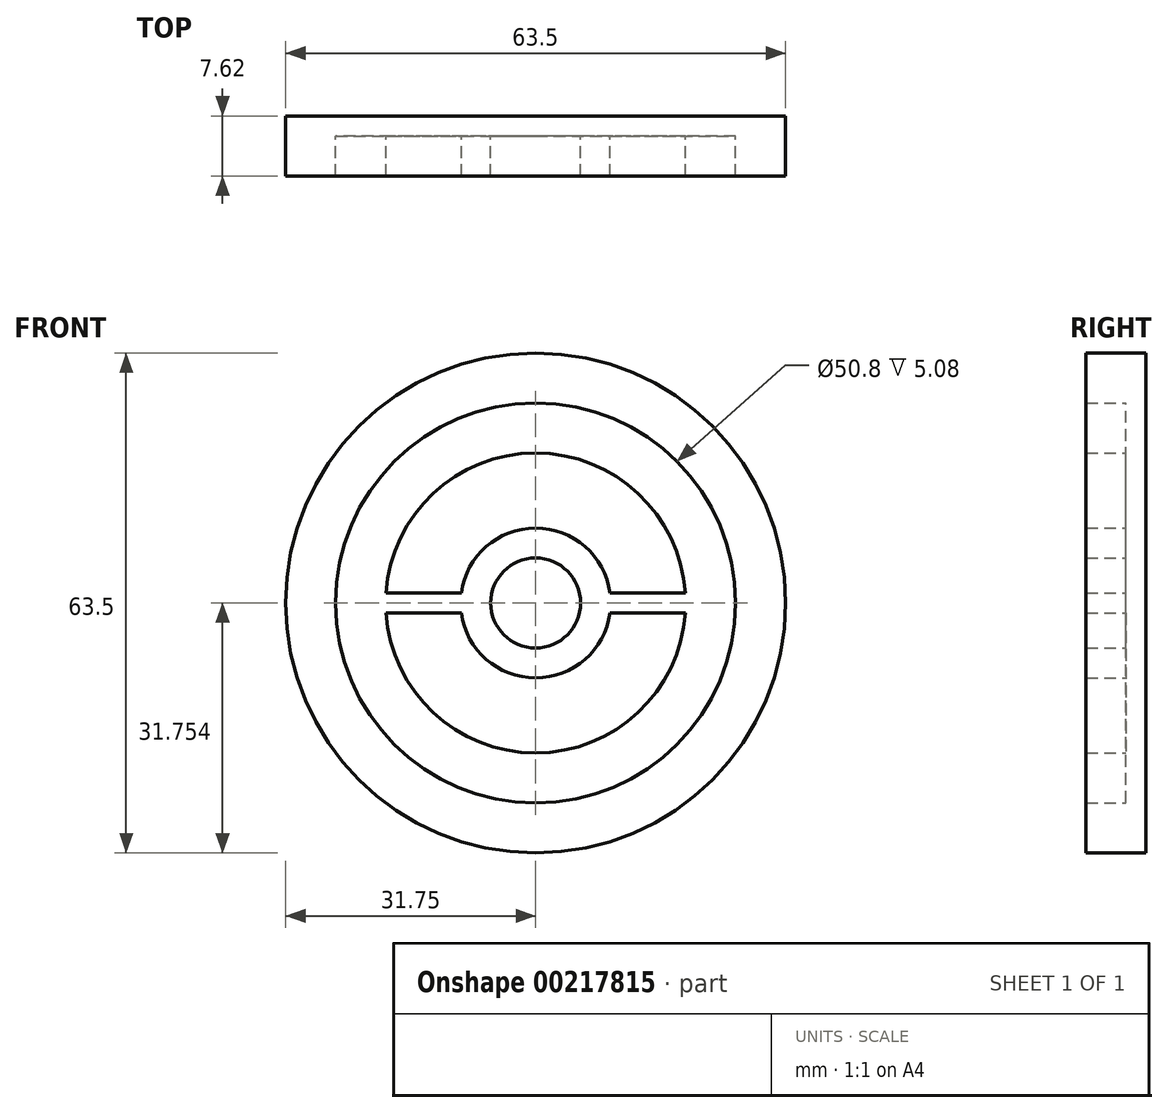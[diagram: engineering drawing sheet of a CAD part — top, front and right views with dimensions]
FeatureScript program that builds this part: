
annotation { "Feature Type Name" : "Feature", "Feature Type Description" : "" }
export const myFeature = defineFeature(function(context is Context, id is Id, definition is map)
    precondition{}
    {
        {
            var Q0;
            Q0=qCreatedBy(makeId("Front.planeOp"),FACE);
            var sketch = newSketch(context, id + "F0", { "sketchPlane" : qUnion([Q0])});
            skCircle(sketch, "E0", {"center": v(0, 3.92) * mm, "radius": 31.75 * mm});
            skArc(sketch, "E1", {"start": v(1.27, 22.93) * mm, "mid": v(-19, 5.2) * mm, "end": v(-1.27, -15.08) * mm});
            skArc(sketch, "E2", {"start": v(-1.27, 9.5) * mm, "mid": v(-5.57, 2.65) * mm, "end": v(1.27, -1.65) * mm});
            skArc(sketch, "E3", {"start": v(1.27, 13.36) * mm, "mid": v(-5.78, 11.5) * mm, "end": v(-9.44, 5.2) * mm});
            skLineSegment(sketch, "E4", {"start": v(-19.05, 3.92) * mm, "end": v(19.05, 3.92) * mm, "construction": true});
            skLineSegment(sketch, "E5.0", {"start": v(-19, 5.2) * mm, "end": v(-9.44, 5.2) * mm});
            skLineSegment(sketch, "E6.0", {"start": v(-19, 2.65) * mm, "end": v(-9.44, 2.65) * mm});
            skLineSegment(sketch, "E7.trimOffspring", {"start": v(9.44, 5.2) * mm, "end": v(19, 5.2) * mm});
            skLineSegment(sketch, "E8.trimOffspring", {"start": v(9.44, 2.65) * mm, "end": v(19, 2.65) * mm});
            skLineSegment(sketch, "E9", {"start": v(0, 13.45) * mm, "end": v(0, -5.6) * mm, "construction": true});
            skLineSegment(sketch, "E10.0", {"start": v(1.27, 13.36) * mm, "end": v(1.27, 9.5) * mm});
            skLineSegment(sketch, "E11.0", {"start": v(-1.27, 13.36) * mm, "end": v(-1.27, 9.5) * mm});
            skArc(sketch, "E12.trimOffspring", {"start": v(9.44, 5.2) * mm, "mid": v(6.74, 10.66) * mm, "end": v(1.27, 13.36) * mm});
            skArc(sketch, "E13.trimOffspring", {"start": v(-9.44, 2.65) * mm, "mid": v(-6.74, -2.81) * mm, "end": v(-1.27, -5.52) * mm});
            skArc(sketch, "E14.trimOffspring", {"start": v(-1.27, -5.52) * mm, "mid": v(5.78, -3.65) * mm, "end": v(9.44, 2.65) * mm});
            skArc(sketch, "E15.trimOffspring", {"start": v(-1.27, -15.08) * mm, "mid": v(19, 2.65) * mm, "end": v(1.27, 22.93) * mm});
            skArc(sketch, "E16.trimOffspring", {"start": v(1.27, -1.65) * mm, "mid": v(5.57, 5.2) * mm, "end": v(-1.27, 9.5) * mm});
            skLineSegment(sketch, "E17.trimOffspring", {"start": v(-1.27, -1.65) * mm, "end": v(-1.27, -5.52) * mm});
            skLineSegment(sketch, "E18.trimOffspring", {"start": v(1.27, -1.65) * mm, "end": v(1.27, -5.52) * mm});
            skLineSegment(sketch, "E19", {"start": v(-1.27, 22.93) * mm, "end": v(-1.27, 29.3) * mm});
            skLineSegment(sketch, "E20", {"start": v(1.27, 22.93) * mm, "end": v(1.27, 29.3) * mm});
            skLineSegment(sketch, "E21.MirrorCS", {"start": v(-1.27, -15.08) * mm, "end": v(-1.27, -21.44) * mm});
            skLineSegment(sketch, "E22.MirrorCS", {"start": v(1.27, -15.08) * mm, "end": v(1.27, -21.44) * mm});
            skArc(sketch, "E23", {"start": v(1.27, 29.3) * mm, "mid": v(-25.4, 3.92) * mm, "end": v(1.27, -21.44) * mm});
            skArc(sketch, "E24.trimOffspring", {"start": v(1.27, -21.44) * mm, "mid": v(25.4, 3.92) * mm, "end": v(1.27, 29.3) * mm});
            skPoint(sketch, "E25.orphan", {"position": v(1.27, -15.08) * mm});
            skSolve(sketch);
        }
        {
            var Q0;
            Q0 = qSketchRegion(id + "F0", true);
            var Q1;
            Q1=makeQuery(id+"F0.imprint","IMPRINT",FACE,{"disambiguationData":[TD([[makeQuery(id+"F0.imprint","IMPRINT",EDGE,{"derivedFrom":sQuery(id+"F0.wireOp",EDGE,"E2")}),1.0]])]});
            var Q2;
            {var subQ0=sQuery(id+"F0.wireOp",EDGE,"E5.0");Q2=makeQuery(id+"F0.imprint","IMPRINT",FACE,{"disambiguationData":[TD([[makeQuery(id+"F0.imprint","IMPRINT",EDGE,{"derivedFrom":subQ0}),1.0]])]});}
            var Q3;
            {var subQ2=sQuery(id+"F0.wireOp",EDGE,"E6.0");Q3=makeQuery(id+"F0.imprint","IMPRINT",FACE,{"disambiguationData":[TD([[makeQuery(id+"F0.imprint","IMPRINT",EDGE,{"derivedFrom":subQ2}),-1.0]])]});}
            extrude(context, id + "F1", {"entities" : qUnion([Q0, Q1, Q2, Q3]), "depth" : 7.62 * mm});
        }
        {
            var Q0;
            {var subQ4=sQuery(id+"F0.wireOp",EDGE,"E19");Q0=makeQuery(id+"F0.imprint","IMPRINT",FACE,{"disambiguationData":[TD([[makeQuery(id+"F0.imprint","IMPRINT",EDGE,{"derivedFrom":subQ4}),1.0]])]});}
            var Q1;
            {var subQ0=sQuery(id+"F0.wireOp",EDGE,"E20");Q1=makeQuery(id+"F0.imprint","IMPRINT",FACE,{"disambiguationData":[TD([[makeQuery(id+"F0.imprint","IMPRINT",EDGE,{"derivedFrom":subQ0}),-1.0]])]});}
            var Q2;
            {var subQ1=sQuery(id+"F0.wireOp",EDGE,"E7.trimOffspring");Q2=makeQuery(id+"F0.imprint","IMPRINT",FACE,{"disambiguationData":[TD([[makeQuery(id+"F0.imprint","IMPRINT",EDGE,{"derivedFrom":subQ1}),-1.0]])]});}
            var Q3;
            {var subQ0=sQuery(id+"F0.wireOp",EDGE,"E5.0");Q3=makeQuery(id+"F0.imprint","IMPRINT",FACE,{"disambiguationData":[TD([[makeQuery(id+"F0.imprint","IMPRINT",EDGE,{"derivedFrom":subQ0}),-1.0]])]});}
            var Q4;
            {var subQ2=sQuery(id+"F0.wireOp",EDGE,"E19");Q4=makeQuery(id+"F0.imprint","IMPRINT",FACE,{"disambiguationData":[TD([[makeQuery(id+"F0.imprint","IMPRINT",EDGE,{"derivedFrom":subQ2}),-1.0]])]});}
            var Q5;
            {var subQ0=sQuery(id+"F0.wireOp",EDGE,"E10.0");Q5=makeQuery(id+"F0.imprint","IMPRINT",FACE,{"disambiguationData":[TD([[makeQuery(id+"F0.imprint","IMPRINT",EDGE,{"derivedFrom":subQ0}),-1.0]])]});}
            var Q6;
            {var subQ2=sQuery(id+"F0.wireOp",EDGE,"E17.trimOffspring");Q6=makeQuery(id+"F0.imprint","IMPRINT",FACE,{"disambiguationData":[TD([[makeQuery(id+"F0.imprint","IMPRINT",EDGE,{"derivedFrom":subQ2}),1.0]])]});}
            var Q7;
            {var subQ0=sQuery(id+"F0.wireOp",EDGE,"E21.MirrorCS");Q7=makeQuery(id+"F0.imprint","IMPRINT",FACE,{"disambiguationData":[TD([[makeQuery(id+"F0.imprint","IMPRINT",EDGE,{"derivedFrom":subQ0}),1.0]])]});}
            extrude(context, id + "F2", {"entities" : qUnion([Q0, Q1, Q2, Q3, Q4, Q5, Q6, Q7]), "operationType" : NewBodyOperationType.ADD, "depth" : 2.54 * mm});
        }
    });
